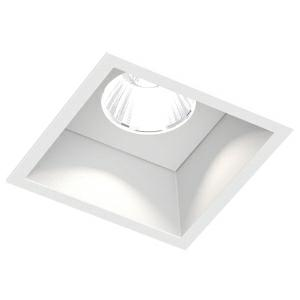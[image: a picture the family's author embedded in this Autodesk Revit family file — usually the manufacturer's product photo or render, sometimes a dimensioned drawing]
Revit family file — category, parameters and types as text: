
# Revit family: 4di_220-0583
name_source: partatom
category: Lighting Fixtures
units: mm (PartAtom-declared; Revit-internal decimal feet)

## family parameters
Cut with Voids When Loaded = No
Host = Face
Light Source = No
Part Type = Normal
Room Calculation Point = No
Round Connector Dimension = Use Diameter
Shared = No

## types (1)
- 220-0583-K20 (1 x LED, 1412.38 lm, 13.8 W, 2700K)
    Apparent Load = 14 VA
    CIE Flux Codes = 99 100 100 100 67
    Color Rendering = 1A/90…99
    Color Temperature = 2700K
    Default Elevation = 1800 mm
    Description = 4DI
    Height = 0 mm  [stored 0 ft]
    Lamp = 1 x LED
    Lamp Light Flux = 1412.38 lm
    Lamp Power = 13.8 W
    Lamp count = 1
    Length = 92 mm
    Luminous efficacy = 69 lm/W
    Manufacturer = Prolicht
    ModVariant = No
    Model = 220-0583
    Mounting Place = Ceiling
    Mounting Type = Recessed
    Number of Poles = 1
    OnlyDefault = Yes
    Power Factor = 1
    Product Name = 4DI
    Product group = Recessed spotlights
    ProductGroupID = 422
    Protection Class = Protection class
    Protection Degree = Degree of protection
    RLX_Detail_Level = 1
    RLX_Emergency_Light_Flux = 0 lm
    RLX_Emergency_Type = 0
    RLX_Emergency_Type_DB = No
    RlxData = <blob elided: 307585 chars, md5=feccbcdd>
    Socket = socket
    Standby Power = 0 W
    System Light Flux = 947 lm
    System Power = 14 W
    Type Comments = REFLECTOR 20° (20)
    Type Image = 220-0583.jpg
    URL = http://relux.com
    VarID = 220-0583-k20
    Voltage = 0 V
    Weight = 0.00 kg
    Width = 92 mm

note: [stored X ft] marks values corroborated as IEEE doubles in the binary element streams (Revit-internal decimal feet)

## geometry (parser evidence)
native form markers: Blend x4, Sweep x11
no freeform markers — native parametric forms only
